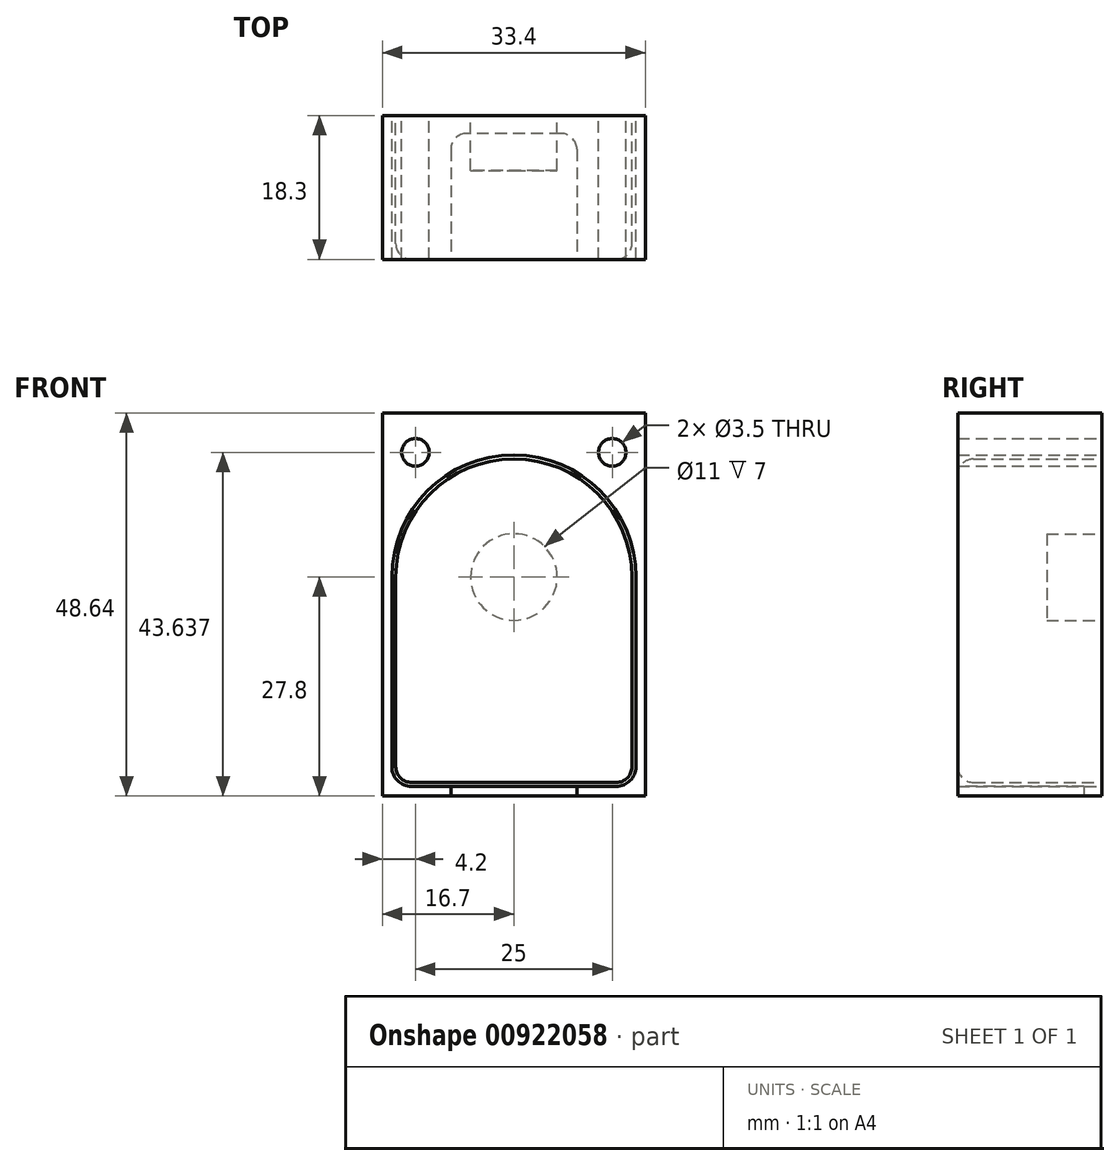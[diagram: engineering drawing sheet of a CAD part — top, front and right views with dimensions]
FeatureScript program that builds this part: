
annotation { "Feature Type Name" : "Feature", "Feature Type Description" : "" }
export const myFeature = defineFeature(function(context is Context, id is Id, definition is map)
    precondition{}
    {
        {
            var Q0;
            Q0=qCreatedBy(makeId("Front.planeOp"),FACE);
            var sketch = newSketch(context, id + "F0", { "sketchPlane" : qUnion([Q0])});
            skLineSegment(sketch, "E0.top", {"start": v(0, 0) * mm, "end": v(30, 0) * mm});
            skLineSegment(sketch, "E0.left", {"start": v(0, 26.1) * mm, "end": v(0, 0) * mm});
            skLineSegment(sketch, "E0.right", {"start": v(30, 26.1) * mm, "end": v(30, 0) * mm});
            skArc(sketch, "E1", {"start": v(30, 26.1) * mm, "mid": v(15, 41.1) * mm, "end": v(0, 26.1) * mm});
            skSolve(sketch);
        }
        {
            var Q0;
            Q0 = qSketchRegion(id + "F0", true);
            extrude(context, id + "F1", {"entities" : qUnion([Q0]), "depth" : 18.3 * mm, "offsetDistance" : 25.4 * mm});
        }
        {
            var Q0;
            Q0=makeQuery(id+"F1.opExtrude","SWEPT_EDGE",EDGE,{"disambiguationData":[OSD([sQuery(id+"F0.wireOp",EDGE,"E0.top"),sQuery(id+"F0.wireOp",EDGE,"E0.right")])]});
            var Q1;
            Q1=makeQuery(id+"F1.opExtrude","SWEPT_EDGE",EDGE,{"disambiguationData":[OSD([sQuery(id+"F0.wireOp",EDGE,"E0.top"),sQuery(id+"F0.wireOp",EDGE,"E0.left")])]});
            var Q2;
            Q2=makeQuery(id+"F1.opExtrude","CAP_FACE",FACE,{"disambiguationData":[OSD([sQuery(id+"F0.wireOp",EDGE,"E0.top"),sQuery(id+"F0.wireOp",EDGE,"E0.left"),sQuery(id+"F0.wireOp",EDGE,"E0.right"),sQuery(id+"F0.wireOp",EDGE,"E1")])],"isStart":false});
            fillet(context, id + "F2", {"entities" : qUnion([Q0, Q1, Q2]), "radius" : 2 * mm, "tangentPropagation" : true, "allowEdgeOverflow" : false});
        }
        {
            var Q0;
            Q0=makeQuery(id+"F1.opExtrude","CAP_FACE",FACE,{"disambiguationData":[OSD([sQuery(id+"F0.wireOp",EDGE,"E0.top"),sQuery(id+"F0.wireOp",EDGE,"E0.left"),sQuery(id+"F0.wireOp",EDGE,"E0.right"),sQuery(id+"F0.wireOp",EDGE,"E1")])],"isStart":true});
            var sketch = newSketch(context, id + "F3", { "sketchPlane" : qUnion([Q0])});
            skCircle(sketch, "E2", {"center": v(-15, 26.1) * mm, "radius": 5.5 * mm});
            skSolve(sketch);
        }
        {
            var Q0;
            Q0 = qSketchRegion(id + "F3", true);
            extrude(context, id + "F4", {"entities" : qUnion([Q0]), "operationType" : NewBodyOperationType.REMOVE, "oppositeDirection" : true, "depth" : 7 * mm, "offsetDistance" : 25.4 * mm});
        }
        {
            var Q0;
            Q0=makeQuery(id+"F1.opExtrude","CAP_FACE",FACE,{"disambiguationData":[OSD([sQuery(id+"F0.wireOp",EDGE,"E0.top"),sQuery(id+"F0.wireOp",EDGE,"E0.left"),sQuery(id+"F0.wireOp",EDGE,"E0.right"),sQuery(id+"F0.wireOp",EDGE,"E1")])],"isStart":true});
            var sketch = newSketch(context, id + "F5", { "sketchPlane" : qUnion([Q0])});
            skArc(sketch, "E3.0", {"start": v(-30.5, 26.1) * mm, "mid": v(-15, 41.6) * mm, "end": v(0.5, 26.1) * mm});
            skArc(sketch, "E3.1", {"start": v(-30.5, 2) * mm, "mid": v(-29.77, 0.23) * mm, "end": v(-28, -0.5) * mm});
            skLineSegment(sketch, "E3.2", {"start": v(-2, -0.5) * mm, "end": v(-28, -0.5) * mm});
            skLineSegment(sketch, "E3.3", {"start": v(-30.5, 26.1) * mm, "end": v(-30.5, 2) * mm});
            skArc(sketch, "E3.4", {"start": v(-2, -0.5) * mm, "mid": v(-0.23, 0.23) * mm, "end": v(0.5, 2) * mm});
            skLineSegment(sketch, "E3.5", {"start": v(0.5, 26.1) * mm, "end": v(0.5, 2) * mm});
            skLineSegment(sketch, "E4.bottom", {"start": v(-31.7, 46.94) * mm, "end": v(1.7, 46.94) * mm});
            skLineSegment(sketch, "E4.top", {"start": v(-31.7, -1.7) * mm, "end": v(1.7, -1.7) * mm});
            skLineSegment(sketch, "E4.left", {"start": v(-31.7, 46.94) * mm, "end": v(-31.7, -1.7) * mm});
            skLineSegment(sketch, "E4.right", {"start": v(1.7, 46.94) * mm, "end": v(1.7, -1.7) * mm});
            skCircle(sketch, "E5", {"center": v(-27.5, 41.94) * mm, "radius": 1.75 * mm});
            skCircle(sketch, "E6", {"center": v(-2.5, 41.94) * mm, "radius": 1.75 * mm});
            skLineSegment(sketch, "E7", {"start": v(-27.5, 41.94) * mm, "end": v(-2.5, 41.94) * mm, "construction": true});
            skPoint(sketch, "E8", {"position": v(-15, 41.94) * mm});
            skSolve(sketch);
        }
        {
            var Q0;
            Q0 = qSketchRegion(id + "F5", true);
            var Q1;
            Q1=makeQuery(id+"F1.opExtrude","CAP_FACE",FACE,{"disambiguationData":[OSD([sQuery(id+"F0.wireOp",EDGE,"E0.top"),sQuery(id+"F0.wireOp",EDGE,"E0.left"),sQuery(id+"F0.wireOp",EDGE,"E0.right"),sQuery(id+"F0.wireOp",EDGE,"E1")])],"isStart":false});
            extrude(context, id + "F6", {"entities" : qUnion([Q0]), "endBound" : BoundingType.UP_TO_SURFACE, "oppositeDirection" : true, "depth" : 25 * mm, "endBoundEntityFace" : qUnion([Q1]), "offsetDistance" : 25 * mm});
        }
        {
            var Q0;
            Q0=makeQuery(id+"F6.opExtrude","CAP_FACE",FACE,{"disambiguationData":[OSD([sQuery(id+"F5.wireOp",EDGE,"E3.0"),sQuery(id+"F5.wireOp",EDGE,"E3.1"),sQuery(id+"F5.wireOp",EDGE,"E3.2"),sQuery(id+"F5.wireOp",EDGE,"E3.3"),sQuery(id+"F5.wireOp",EDGE,"E3.4"),sQuery(id+"F5.wireOp",EDGE,"E3.5"),sQuery(id+"F5.wireOp",EDGE,"E4.bottom"),sQuery(id+"F5.wireOp",EDGE,"E4.top"),sQuery(id+"F5.wireOp",EDGE,"E4.left"),sQuery(id+"F5.wireOp",EDGE,"E4.right"),sQuery(id+"F5.wireOp",EDGE,"E5"),sQuery(id+"F5.wireOp",EDGE,"E6")])],"isStart":false});
            var sketch = newSketch(context, id + "F7", { "sketchPlane" : qUnion([Q0])});
            skLineSegment(sketch, "E9.bottom", {"start": v(7, -0.5) * mm, "end": v(23, -0.5) * mm});
            skLineSegment(sketch, "E9.top", {"start": v(7, -1.7) * mm, "end": v(23, -1.7) * mm});
            skLineSegment(sketch, "E9.left", {"start": v(7, -0.5) * mm, "end": v(7, -1.7) * mm});
            skLineSegment(sketch, "E9.right", {"start": v(23, -0.5) * mm, "end": v(23, -1.7) * mm});
            skPoint(sketch, "E10", {"position": v(15, -1.7) * mm});
            skSolve(sketch);
        }
        {
            var Q0;
            Q0 = qSketchRegion(id + "F7", true);
            extrude(context, id + "F8", {"entities" : qUnion([Q0]), "operationType" : NewBodyOperationType.REMOVE, "oppositeDirection" : true, "depth" : 16 * mm, "offsetDistance" : 25 * mm});
        }
        {
            var Q0;
            Q0=makeQuery(id+"F8.boolean.opBoolean","COPY",EDGE,{"derivedFrom":makeQuery(id+"F8.opExtrude","CAP_EDGE",EDGE,{"disambiguationData":[OSD([sQuery(id+"F7.wireOp",EDGE,"E9.left")])],"isStart":true})});
            var Q1;
            Q1=makeQuery(id+"F8.boolean.opBoolean","COPY",EDGE,{"derivedFrom":makeQuery(id+"F8.opExtrude","CAP_EDGE",EDGE,{"disambiguationData":[OSD([sQuery(id+"F7.wireOp",EDGE,"E9.right")])],"isStart":true})});
            var Q2;
            Q2=makeQuery(id+"F8.boolean.opBoolean","COPY",EDGE,{"derivedFrom":makeQuery(id+"F8.opExtrude","CAP_EDGE",EDGE,{"disambiguationData":[OSD([sQuery(id+"F7.wireOp",EDGE,"E9.left")])],"isStart":false})});
            var Q3;
            Q3=makeQuery(id+"F8.boolean.opBoolean","COPY",EDGE,{"derivedFrom":makeQuery(id+"F8.opExtrude","CAP_EDGE",EDGE,{"disambiguationData":[OSD([sQuery(id+"F7.wireOp",EDGE,"E9.right")])],"isStart":false})});
            fillet(context, id + "F9", {"entities" : qUnion([Q0, Q1, Q2, Q3]), "radius" : 2 * mm, "tangentPropagation" : true, "allowEdgeOverflow" : false});
        }
    });
